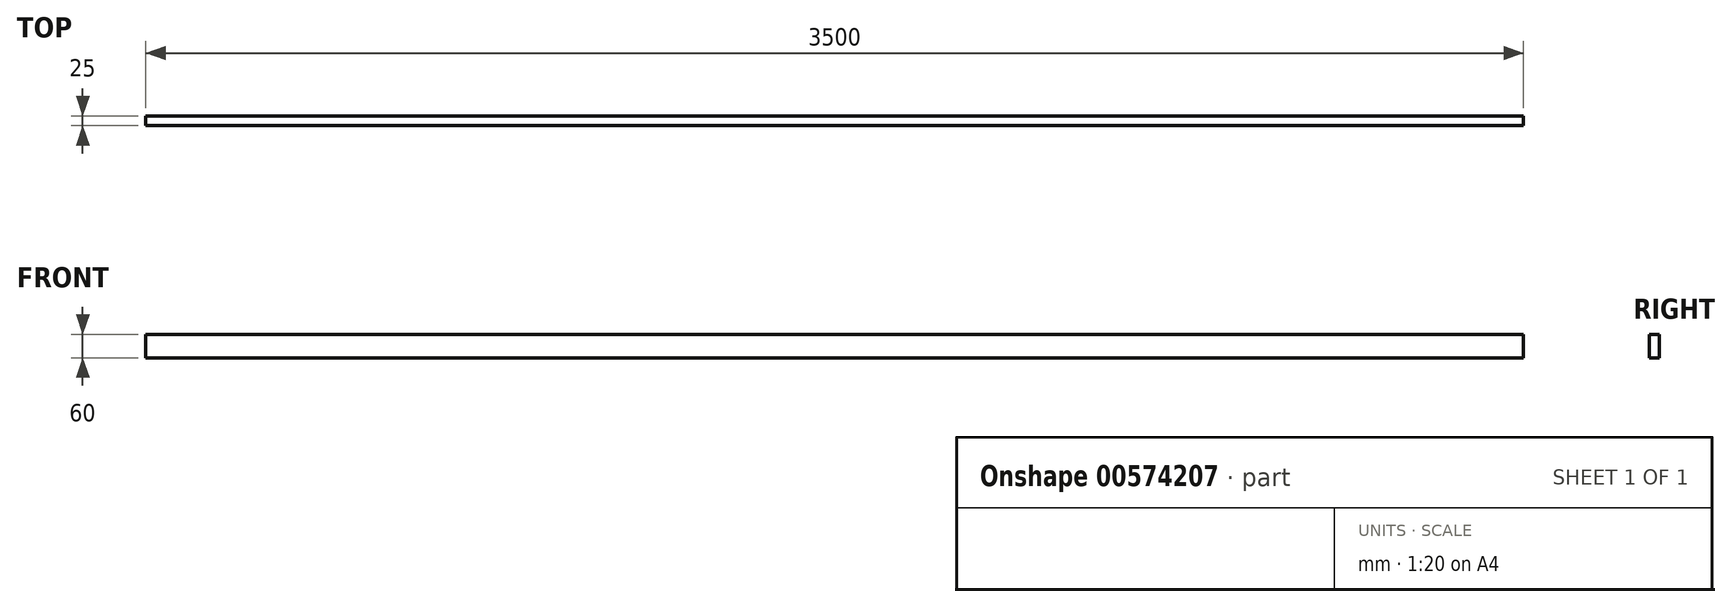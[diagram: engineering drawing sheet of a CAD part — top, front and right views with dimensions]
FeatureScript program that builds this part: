
annotation { "Feature Type Name" : "Feature", "Feature Type Description" : "" }
export const myFeature = defineFeature(function(context is Context, id is Id, definition is map)
    precondition{}
    {
        {
            var Q0;
            Q0=qCreatedBy(makeId("Right.planeOp"),FACE);
            var sketch = newSketch(context, id + "F0", { "sketchPlane" : qUnion([Q0])});
            skLineSegment(sketch, "E0.bottom", {"start": v(0, 0) * mm, "end": v(-25, 0) * mm});
            skLineSegment(sketch, "E0.top", {"start": v(0, 60) * mm, "end": v(-25, 60) * mm});
            skLineSegment(sketch, "E0.left", {"start": v(0, 0) * mm, "end": v(0, 60) * mm});
            skLineSegment(sketch, "E0.right", {"start": v(-25, 0) * mm, "end": v(-25, 60) * mm});
            skSolve(sketch);
        }
        {
            var Q0;
            Q0=makeQuery(id+"F0.imprint","IMPRINT",FACE,{"disambiguationData":[TD([[makeQuery(id+"F0.imprint","IMPRINT",EDGE,{"derivedFrom":sQuery(id+"F0.wireOp",EDGE,"E0.bottom")}),-1.0]])]});
            extrude(context, id + "F1", {"entities" : qUnion([Q0]), "depth" : 3500 * mm, "offsetDistance" : 25 * mm});
        }
    });
